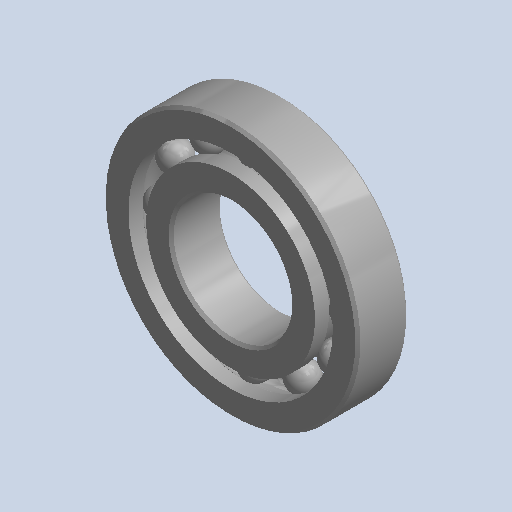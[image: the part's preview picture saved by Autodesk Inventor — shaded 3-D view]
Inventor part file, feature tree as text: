
AUTODESK INVENTOR PART (.ipt)
format: ipt  version: 2022.3 (Build 263350000, 350)  size: 501,760 bytes
history: mixed  units: mm (DEFAULTED — no unit token found)
features: other x11, revolve x3, imported_body x1
ambient origin geometry x8: Origin, YZ Plane, XZ Plane, XY Plane, X Axis, Y Axis, Z Axis, Center Point
bodies: Solid1 (imported_parasolid), Solid2 (imported_parasolid), Solid3 (imported_parasolid), Solid4 (imported_parasolid), Solid5 (imported_parasolid), Solid6 (imported_parasolid), Solid7 (imported_parasolid), Solid8 (imported_parasolid), Solid9 (imported_parasolid), Solid10 (imported_parasolid), Solid11 (imported_parasolid), Solid12 (imported_parasolid), Solid13 (imported_parasolid), Solid14 (imported_parasolid)
feature tree (15):
  revolve  "Revolve1"  [1 undecoded]
  revolve  "Revolve3"  [1 undecoded]
  revolve  "Revolve4"  [1 undecoded]
  other  "CirPattern1[1]"
  other  "CirPattern1[2]"
  other  "CirPattern1[3]"
  other  "CirPattern1[4]"
  other  "CirPattern1[5]"
  other  "CirPattern1[6]"
  other  "CirPattern1[7]"
  other  "CirPattern1[8]"
  other  "CirPattern1[9]"
  other  "CirPattern1[10]"
  other  "CirPattern1[11]"
  imported_body  NMx_Import_Brep_tag  [imported B-rep: ~28 faces, bbox_mm=[12.7, 0.0, 9.525]]
note: 3 required parameter values undecoded (feature->parameter linkage not recoverable at this tier; creation-order binding heuristic only, values carry confidence <= 0.55)
